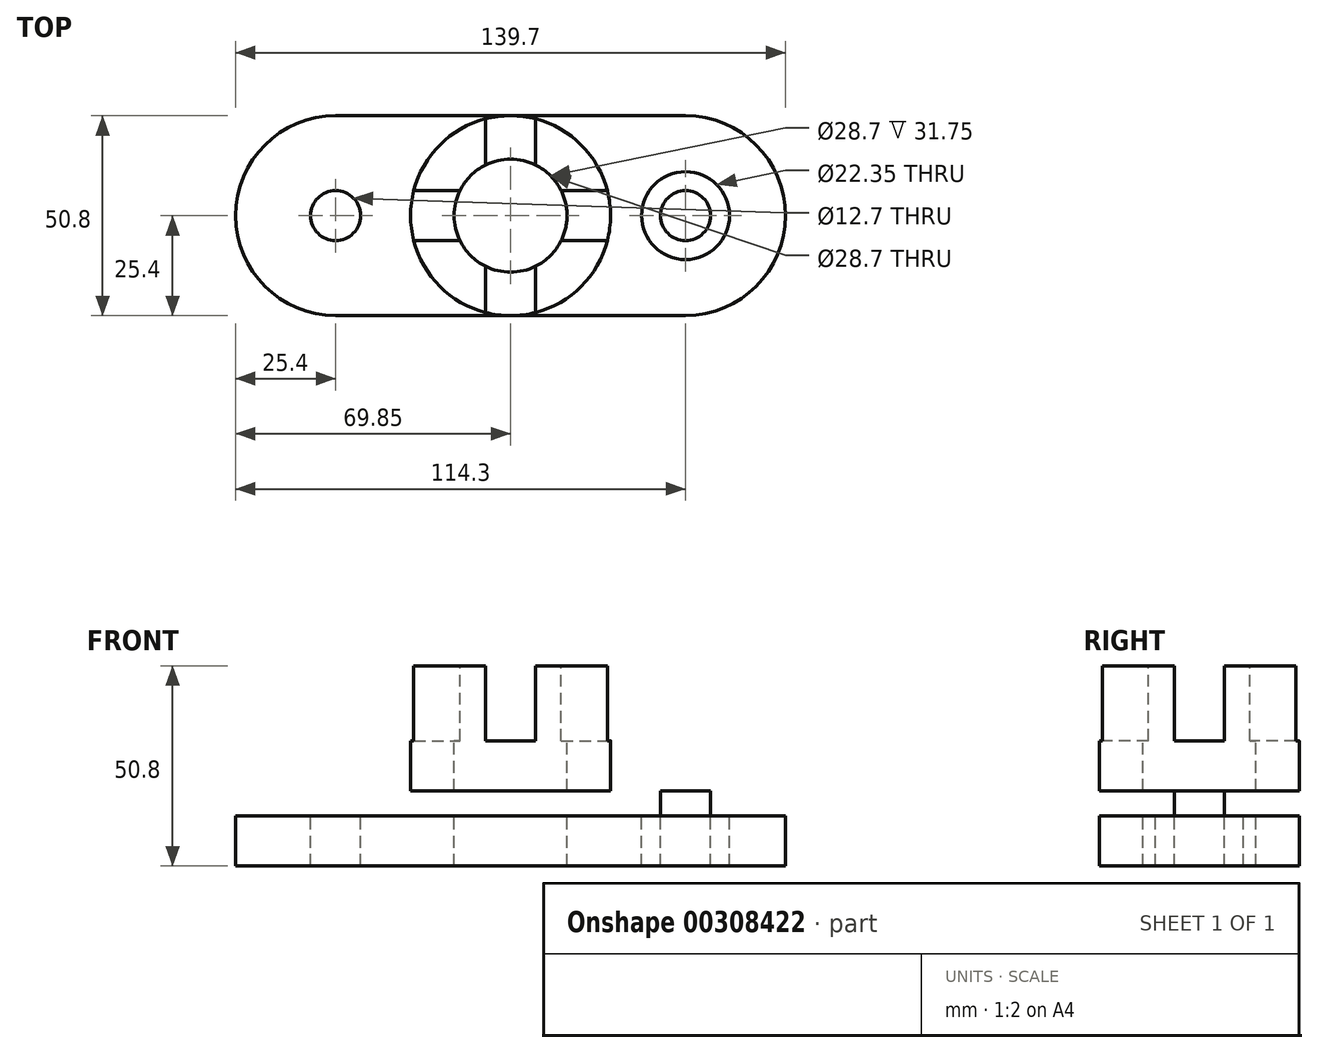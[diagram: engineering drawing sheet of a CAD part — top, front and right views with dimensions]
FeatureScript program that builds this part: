
annotation { "Feature Type Name" : "Feature", "Feature Type Description" : "" }
export const myFeature = defineFeature(function(context is Context, id is Id, definition is map)
    precondition{}
    {
        {
            var Q0;
            Q0=qCreatedBy(makeId("Top.planeOp"),FACE);
            var sketch = newSketch(context, id + "F0", { "sketchPlane" : qUnion([Q0])});
            skArc(sketch, "E0", {"start": v(-44.45, 25.4) * mm, "mid": v(-69.85, 0) * mm, "end": v(-44.45, -25.4) * mm});
            skArc(sketch, "E1", {"start": v(44.45, -25.4) * mm, "mid": v(69.85, 0) * mm, "end": v(44.45, 25.4) * mm});
            skLineSegment(sketch, "E2", {"start": v(-44.45, 25.4) * mm, "end": v(44.45, 25.4) * mm});
            skLineSegment(sketch, "E3", {"start": v(-44.45, -25.4) * mm, "end": v(44.45, -25.4) * mm});
            skSolve(sketch);
        }
        {
            var Q0;
            Q0 = qSketchRegion(id + "F0", true);
            extrude(context, id + "F1", {"entities" : qUnion([Q0]), "oppositeDirection" : true, "depth" : 19.05 * mm});
        }
        {
            var Q0;
            Q0=makeQuery(id+"F1.opExtrude","CAP_FACE",FACE,{"disambiguationData":[OSD([sQuery(id+"F0.wireOp",EDGE,"E0"),sQuery(id+"F0.wireOp",EDGE,"E1"),sQuery(id+"F0.wireOp",EDGE,"E2"),sQuery(id+"F0.wireOp",EDGE,"E3")])],"isStart":true});
            var sketch = newSketch(context, id + "F2", { "sketchPlane" : qUnion([Q0])});
            skLineSegment(sketch, "E4", {"start": v(0, 43.34) * mm, "end": v(0, -45.58) * mm, "construction": true});
            skCircle(sketch, "E5", {"center": v(-44.45, 0) * mm, "radius": 11.18 * mm});
            skCircle(sketch, "E6", {"center": v(-44.45, 0) * mm, "radius": 6.35 * mm});
            skCircle(sketch, "E7.MirrorC", {"center": v(44.45, 0) * mm, "radius": 11.18 * mm});
            skCircle(sketch, "E8.MirrorC", {"center": v(44.45, 0) * mm, "radius": 6.35 * mm});
            skSolve(sketch);
        }
        {
            var Q0;
            Q0=makeQuery(id+"F2.imprint","IMPRINT",FACE,{"disambiguationData":[TD([[makeQuery(id+"F2.imprint","IMPRINT",EDGE,{"derivedFrom":sQuery(id+"F2.wireOp",EDGE,"E6")}),1.0]])]});
            var Q1;
            Q1=makeQuery(id+"F2.imprint","IMPRINT",FACE,{"disambiguationData":[TD([[makeQuery(id+"F2.imprint","IMPRINT",EDGE,{"derivedFrom":sQuery(id+"F2.wireOp",EDGE,"E8.MirrorC")}),-1.0]])]});
            extrude(context, id + "F3", {"entities" : qUnion([Q0, Q1]), "operationType" : NewBodyOperationType.REMOVE, "endBound" : BoundingType.THROUGH_ALL, "oppositeDirection" : true, "depth" : 25.4 * mm});
        }
        {
            var Q0;
            Q0=makeQuery(id+"F2.imprint","IMPRINT",FACE,{"disambiguationData":[TD([[makeQuery(id+"F2.imprint","IMPRINT",EDGE,{"derivedFrom":sQuery(id+"F2.wireOp",EDGE,"E5")}),1.0]])]});
            var Q1;
            Q1=makeQuery(id+"F2.imprint","IMPRINT",FACE,{"disambiguationData":[TD([[makeQuery(id+"F2.imprint","IMPRINT",EDGE,{"derivedFrom":sQuery(id+"F2.wireOp",EDGE,"E7.MirrorC")}),-1.0]])]});
            extrude(context, id + "F4", {"entities" : qUnion([Q0, Q1]), "operationType" : NewBodyOperationType.REMOVE, "oppositeDirection" : true, "depth" : 6.35 * mm});
        }
        {
            var Q0;
            Q0=makeQuery(id+"F1.opExtrude","CAP_FACE",FACE,{"disambiguationData":[OSD([sQuery(id+"F0.wireOp",EDGE,"E0"),sQuery(id+"F0.wireOp",EDGE,"E1"),sQuery(id+"F0.wireOp",EDGE,"E2"),sQuery(id+"F0.wireOp",EDGE,"E3")])],"isStart":true});
            var sketch = newSketch(context, id + "F5", { "sketchPlane" : qUnion([Q0])});
            skCircle(sketch, "E9", {"center": v(0, 0) * mm, "radius": 25.4 * mm});
            skSolve(sketch);
        }
        {
            var Q0;
            Q0 = qSketchRegion(id + "F5", true);
            extrude(context, id + "F6", {"entities" : qUnion([Q0]), "operationType" : NewBodyOperationType.ADD, "depth" : 31.75 * mm});
        }
        {
            var Q0;
            Q0=makeQuery(id+"F6.opExtrude","CAP_FACE",FACE,{"disambiguationData":[OSD([sQuery(id+"F5.wireOp",EDGE,"E9")])],"isStart":false});
            var sketch = newSketch(context, id + "F7", { "sketchPlane" : qUnion([Q0])});
            skCircle(sketch, "E10", {"center": v(0, 0) * mm, "radius": 14.35 * mm});
            skSolve(sketch);
        }
        {
            var Q0;
            Q0 = qSketchRegion(id + "F7", true);
            extrude(context, id + "F8", {"entities" : qUnion([Q0]), "operationType" : NewBodyOperationType.REMOVE, "endBound" : BoundingType.THROUGH_ALL, "oppositeDirection" : true, "depth" : 25.4 * mm});
        }
        {
            var Q0;
            Q0=qCreatedBy(makeId("Right.planeOp"),FACE);
            cPlane(context, id + "F9", {"entities" : qUnion([Q0]), "cplaneType" : CPlaneType.OFFSET, "offset" : 50.8 * mm, "width" : 152.4 * mm, "height" : 152.4 * mm});
        }
        {
            var Q0;
            Q0=qCreatedBy(id+"F9.planeOp",FACE);
            var sketch = newSketch(context, id + "F10", { "sketchPlane" : qUnion([Q0])});
            skLineSegment(sketch, "E11.bottom", {"start": v(-6.35, 31.75) * mm, "end": v(6.35, 31.75) * mm});
            skLineSegment(sketch, "E11.top", {"start": v(-6.35, 12.7) * mm, "end": v(6.35, 12.7) * mm});
            skLineSegment(sketch, "E11.left", {"start": v(-6.35, 31.75) * mm, "end": v(-6.35, 12.7) * mm});
            skLineSegment(sketch, "E11.right", {"start": v(6.35, 31.75) * mm, "end": v(6.35, 12.7) * mm});
            skSolve(sketch);
        }
        {
            var Q0;
            Q0 = qSketchRegion(id + "F10", true);
            extrude(context, id + "F11", {"entities" : qUnion([Q0]), "operationType" : NewBodyOperationType.REMOVE, "endBound" : BoundingType.THROUGH_ALL, "oppositeDirection" : true, "depth" : 25.4 * mm});
        }
        {
            var Q0;
            Q0=qCreatedBy(makeId("Front.planeOp"),FACE);
            cPlane(context, id + "F12", {"entities" : qUnion([Q0]), "cplaneType" : CPlaneType.OFFSET, "offset" : 52.07 * mm, "width" : 152.4 * mm, "height" : 152.4 * mm});
        }
        {
            var Q0;
            Q0=qCreatedBy(id+"F12.planeOp",FACE);
            var sketch = newSketch(context, id + "F13", { "sketchPlane" : qUnion([Q0])});
            skLineSegment(sketch, "E12.bottom", {"start": v(-6.35, 31.75) * mm, "end": v(6.35, 31.75) * mm});
            skLineSegment(sketch, "E12.top", {"start": v(-6.35, 12.7) * mm, "end": v(6.35, 12.7) * mm});
            skLineSegment(sketch, "E12.left", {"start": v(-6.35, 31.75) * mm, "end": v(-6.35, 12.7) * mm});
            skLineSegment(sketch, "E12.right", {"start": v(6.35, 31.75) * mm, "end": v(6.35, 12.7) * mm});
            skSolve(sketch);
        }
        {
            var Q0;
            Q0 = qSketchRegion(id + "F13", true);
            extrude(context, id + "F14", {"entities" : qUnion([Q0]), "operationType" : NewBodyOperationType.REMOVE, "endBound" : BoundingType.THROUGH_ALL, "oppositeDirection" : true, "depth" : 25.4 * mm});
        }
    });
